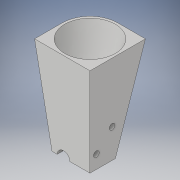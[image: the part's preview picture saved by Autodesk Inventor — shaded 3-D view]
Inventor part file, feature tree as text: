
AUTODESK INVENTOR PART (.ipt)
format: ipt  version: 2018 (Build 220112000, 112)  size: 186,880 bytes
history: native  units: in
note: dims shown in document units (in); Inventor stores cm internally (conversion verified against a paired STEP export)
features: sketch x6, loft x2, extrude x2, plane x1
ambient origin geometry x8: Origin, YZ Plane, XZ Plane, XY Plane, X Axis, Y Axis, Z Axis, Center Point
bodies: Solid1 (feature_tree)
feature tree (11):
  sketch  "Sketch1"  dims[d1=0.8in d2=1.2in]
  plane  "Work Plane1"
  loft  "Loft1"
  loft  "Loft2"
  extrude  "Extrusion1"  Depth=0.875in
  extrude  "Extrusion3"  TaperAngle=0.0deg  [1 undecoded]
  sketch  "Sketch3"  dims[d4=0.4in d5=2.8in]
  sketch  "Sketch4"  dims[d15=0.875in d17=0.875in]
  sketch  "Sketch5"  dims[d18=0.875in d19=0.0in d20=90.0deg]
  sketch  "Sketch6"  dims[d21=0.0in d22=90.0deg]
  sketch  "Sketch8"  dims[d23=1.6in d24=0.875in d26=0.875in d27=0.65in d28=0.0in d29=90.0deg d30=0.0in d31=90.0deg d32=0.4in d33=0.4in d34=0.4in d35=0.2in d36=0.0in d38=3.0in d39=0.0in d42=0.0in d43=0.25in d44=0.32in d46=0.18in d47=0.2in d48=0.18in d49=0.5in d50=0.5in d51=1.0in d52=0.0in d57=0.15in]
note: 1 required parameter value undecoded (feature->parameter linkage not recoverable at this tier; creation-order binding heuristic only, values carry confidence <= 0.55)
